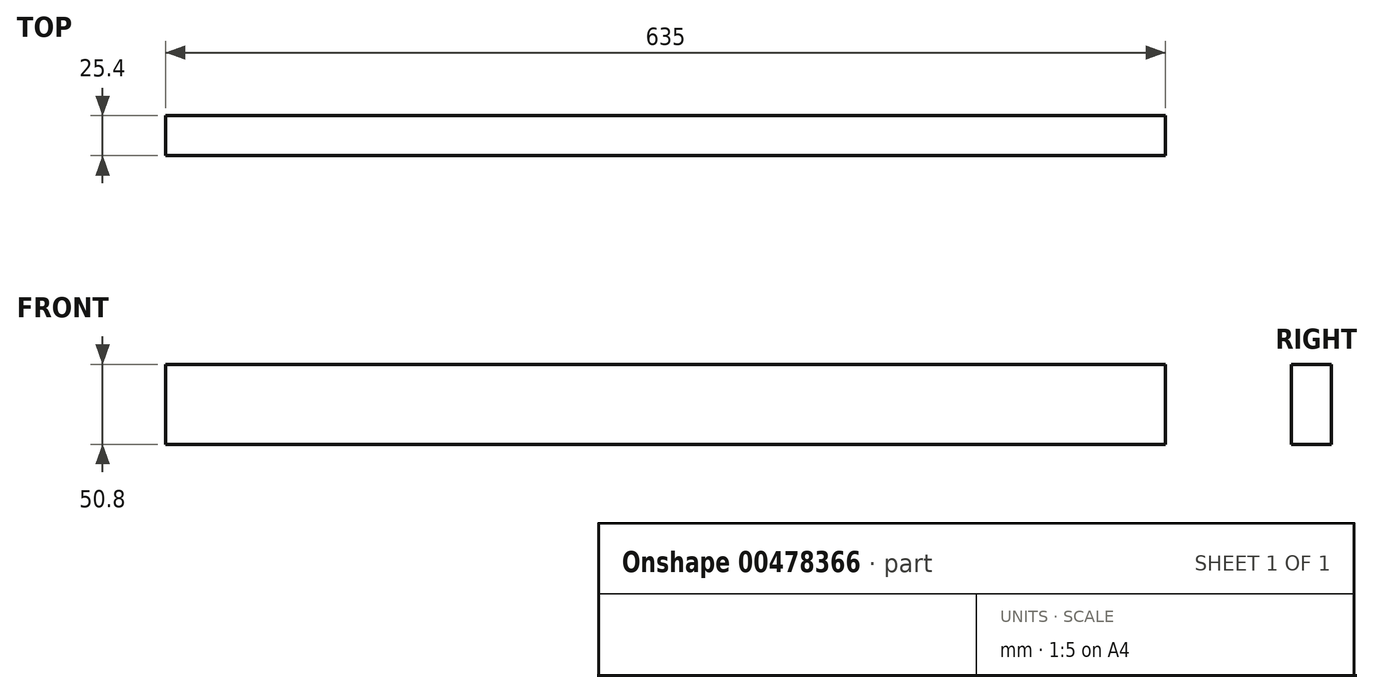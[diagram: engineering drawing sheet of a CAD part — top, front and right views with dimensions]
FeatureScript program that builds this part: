
annotation { "Feature Type Name" : "Feature", "Feature Type Description" : "" }
export const myFeature = defineFeature(function(context is Context, id is Id, definition is map)
    precondition{}
    {
        {
            var Q0;
            Q0=qCreatedBy(makeId("Front.planeOp"),FACE);
            var sketch = newSketch(context, id + "F0", { "sketchPlane" : qUnion([Q0])});
            skLineSegment(sketch, "E0.bottom", {"start": v(-305.4, -74.07) * mm, "end": v(329.6, -74.07) * mm});
            skLineSegment(sketch, "E0.top", {"start": v(-305.4, -23.27) * mm, "end": v(329.6, -23.27) * mm});
            skLineSegment(sketch, "E0.left", {"start": v(-305.4, -74.07) * mm, "end": v(-305.4, -23.27) * mm});
            skLineSegment(sketch, "E0.right", {"start": v(329.6, -74.07) * mm, "end": v(329.6, -23.27) * mm});
            skSolve(sketch);
        }
        {
            var Q0;
            Q0 = qSketchRegion(id + "F0", true);
            extrude(context, id + "F1", {"entities" : qUnion([Q0]), "depth" : 25.4 * mm, "offsetDistance" : 25.4 * mm});
        }
    });
